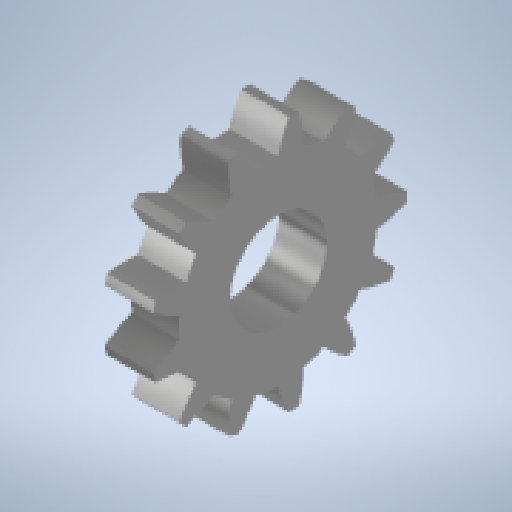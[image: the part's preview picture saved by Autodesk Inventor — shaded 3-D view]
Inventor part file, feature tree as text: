
AUTODESK INVENTOR PART (.ipt)
format: ipt  version: 2025.2 (Build 292293000, 293)  size: 324,608 bytes
history: native  units: in
note: dims shown in document units (in); Inventor stores cm internally (conversion verified against a paired STEP export)
features: other x4, extrude x1, pattern_circular x1
ambient origin geometry x8: Origin, YZ Plane, XZ Plane, XY Plane, X Axis, Y Axis, Z Axis, Center Point
bodies: Volumenkörper1 (feature_tree)
feature tree (6):
  other  "Skelett_Laufkatze.ipt"
  other  "Rohling_Zahnrad"
  extrude  "Zahngeometrie"  Depth=0.3937in
  pattern_circular  "Anzahl_zähne"  Angle=90.0deg  [1 undecoded]
  other  "Zahnrad_Zahnrad_seite"
  other  "Zahnrad_Zahnrad_front"
note: 1 required parameter value undecoded (feature->parameter linkage not recoverable at this tier; creation-order binding heuristic only, values carry confidence <= 0.55)
